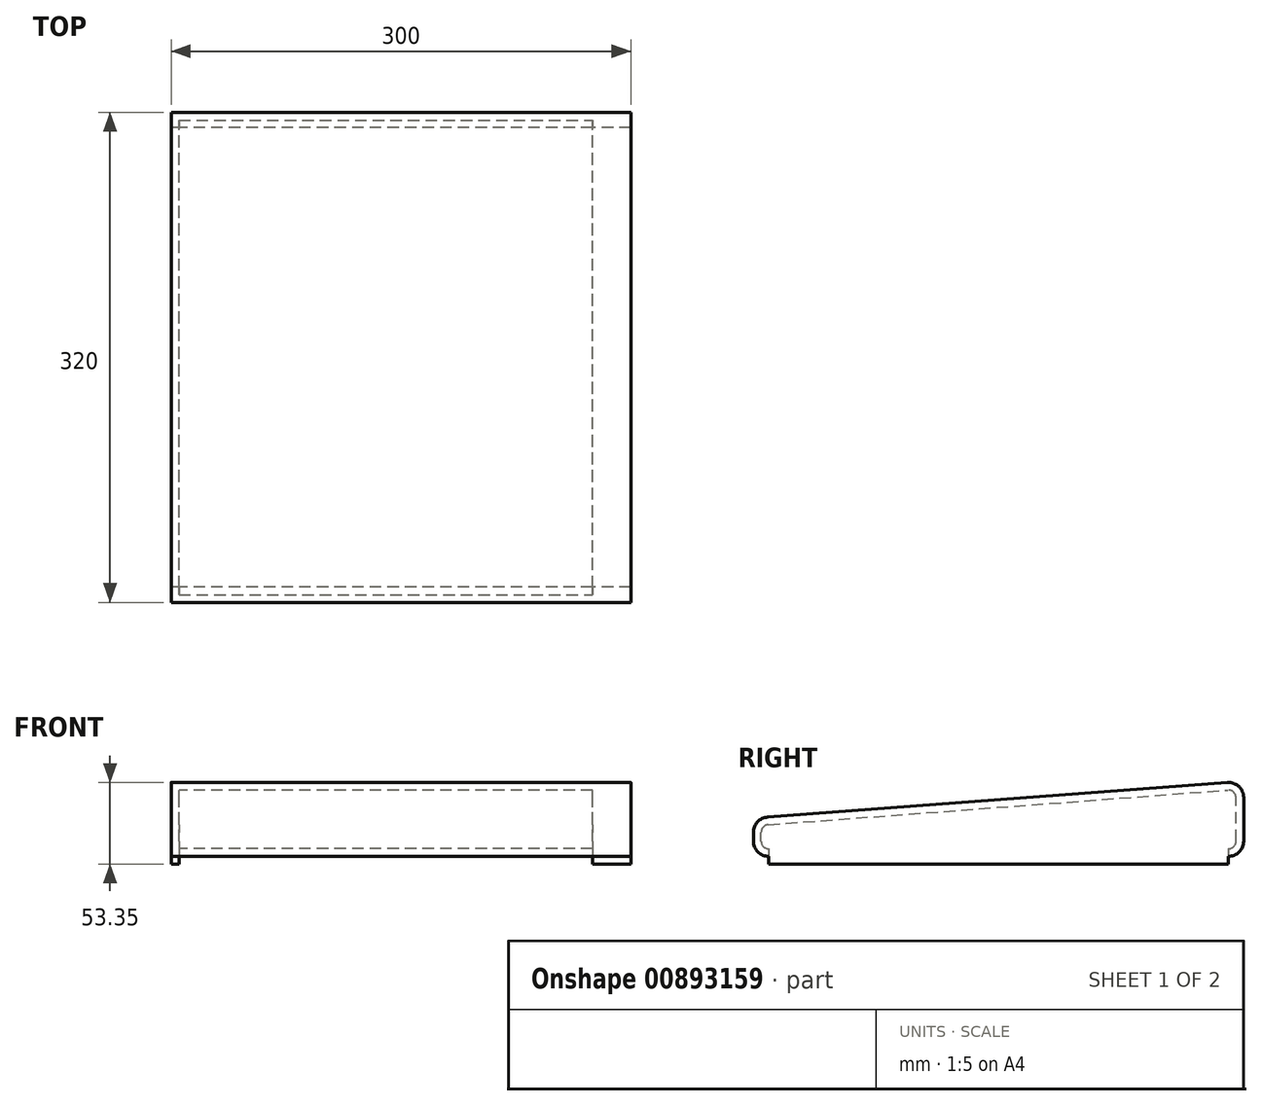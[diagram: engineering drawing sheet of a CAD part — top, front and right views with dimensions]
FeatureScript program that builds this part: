
annotation { "Feature Type Name" : "Feature", "Feature Type Description" : "" }
export const myFeature = defineFeature(function(context is Context, id is Id, definition is map)
    precondition{}
    {
        {
            var Q0;
            Q0=qCreatedBy(makeId("Right.planeOp"),FACE);
            var sketch = newSketch(context, id + "F0", { "sketchPlane" : qUnion([Q0])});
            skLineSegment(sketch, "E0", {"start": v(-351.34, -25) * mm, "end": v(-51.34, -25) * mm});
            skLineSegment(sketch, "E1", {"start": v(-361.34, -15) * mm, "end": v(-361.34, -9.27) * mm});
            skLineSegment(sketch, "E2", {"start": v(-41.34, -15) * mm, "end": v(-41.34, 13.35) * mm});
            skLineSegment(sketch, "E3", {"start": v(-352.1, 0.7) * mm, "end": v(-52.1, 23.32) * mm});
            skPoint(sketch, "E4.visualSharp", {"position": v(-361.34, 0) * mm});
            skArc(sketch, "E4.filletArc", {"start": v(-352.1, 0.7) * mm, "mid": v(-358.67, -2.47) * mm, "end": v(-361.34, -9.27) * mm});
            skPoint(sketch, "E5.visualSharp", {"position": v(-361.34, -25) * mm});
            skArc(sketch, "E5.filletArc", {"start": v(-361.34, -15) * mm, "mid": v(-358.4, -22.07) * mm, "end": v(-351.34, -25) * mm});
            skPoint(sketch, "E6.visualSharp", {"position": v(-41.34, 24.14) * mm});
            skArc(sketch, "E6.filletArc", {"start": v(-41.34, 13.35) * mm, "mid": v(-44.54, 20.69) * mm, "end": v(-52.1, 23.32) * mm});
            skPoint(sketch, "E7.visualSharp", {"position": v(-41.34, -25) * mm});
            skArc(sketch, "E7.filletArc", {"start": v(-51.34, -25) * mm, "mid": v(-44.27, -22.07) * mm, "end": v(-41.34, -15) * mm});
            skSolve(sketch);
        }
        {
            var Q0;
            Q0=makeQuery(id+"F0.imprint","IMPRINT",FACE,{"disambiguationData":[TD([[makeQuery(id+"F0.imprint","IMPRINT",EDGE,{"derivedFrom":sQuery(id+"F0.wireOp",EDGE,"E0")}),1.0]])]});
            extrude(context, id + "F1", {"entities" : qUnion([Q0]), "depth" : 300 * mm, "offsetDistance" : 25 * mm});
        }
        {
            var Q0;
            Q0=makeQuery(id+"F1.opExtrude","SWEPT_FACE",FACE,{"disambiguationData":[OSD([sQuery(id+"F0.wireOp",EDGE,"E0")])]});
            shell(context, id + "F2", {"entities" : qUnion([Q0]), "thickness" : 5 * mm});
        }
        {
            var Q0;
            Q0=makeQuery(id+"F1.opExtrude","CAP_FACE",FACE,{"disambiguationData":[OSD([sQuery(id+"F0.wireOp",EDGE,"E0"),sQuery(id+"F0.wireOp",EDGE,"E1"),sQuery(id+"F0.wireOp",EDGE,"E2"),sQuery(id+"F0.wireOp",EDGE,"E3"),sQuery(id+"F0.wireOp",EDGE,"E4.filletArc"),sQuery(id+"F0.wireOp",EDGE,"E5.filletArc"),sQuery(id+"F0.wireOp",EDGE,"E6.filletArc"),sQuery(id+"F0.wireOp",EDGE,"E7.filletArc")])],"isStart":false});
            var sketch = newSketch(context, id + "F3", { "sketchPlane" : qUnion([Q0])});
            skSolve(sketch);
        }
        {
            var Q0;
            Q0=makeQuery(id+"FV86FQ9cfDMdF77_1.boolean.opBoolean","SPLIT",FACE,{"disambiguationData":[TD([makeQuery(id+"FV86FQ9cfDMdF77_1.opExtrude","SWEPT_FACE",FACE,{"disambiguationData":[OSD([sQuery(id+"F3.wireOp",EDGE,"lBtMn5sw-AZNF-spVU-DaEl-DQMSO4VxvqlR")])]})])],"derivedFrom":makeQuery(id+"F1.opExtrude","CAP_FACE",FACE,{"disambiguationData":[OSD([sQuery(id+"F0.wireOp",EDGE,"E0"),sQuery(id+"F0.wireOp",EDGE,"E1"),sQuery(id+"F0.wireOp",EDGE,"E2"),sQuery(id+"F0.wireOp",EDGE,"E3"),sQuery(id+"F0.wireOp",EDGE,"E4.filletArc"),sQuery(id+"F0.wireOp",EDGE,"E5.filletArc"),sQuery(id+"F0.wireOp",EDGE,"E6.filletArc"),sQuery(id+"F0.wireOp",EDGE,"E7.filletArc")])],"isStart":false})});
            extrude(context, id + "F4", {"entities" : qUnion([Q0]), "operationType" : NewBodyOperationType.ADD, "oppositeDirection" : true, "depth" : 25 * mm, "offsetDistance" : 25 * mm});
        }
        {
            var Q0;
            Q0=makeQuery(id+"F2.opShell","OFFSET_FACE",FACE,{"disambiguationData":[OSD([sQuery(id+"F0.wireOp",EDGE,"E3")])]});
            var sketch = newSketch(context, id + "F5", { "sketchPlane" : qUnion([Q0])});
            skSolve(sketch);
        }
        {
            var Q0;
            Q0=qSketchRegion(id+"F5",true);
            var Q1;
            Q1=makeQuery(id+"F2.opShell","OFFSET_FACE",FACE,{"disambiguationData":[OSD([sQuery(id+"F0.wireOp",EDGE,"E0")])]});
            extrude(context, id + "F6", {"entities" : qUnion([Q0, Q1]), "operationType" : NewBodyOperationType.ADD, "depth" : 5 * mm, "offsetDistance" : 25 * mm});
        }
        {
            var Q0;
            Q0=makeQuery(id+"F1.opExtrude","SWEPT_FACE",FACE,{"disambiguationData":[OSD([sQuery(id+"F0.wireOp",EDGE,"E0")])]});
            extrude(context, id + "F7", {"entities" : qUnion([Q0]), "operationType" : NewBodyOperationType.ADD, "depth" : 5 * mm, "offsetDistance" : 25 * mm});
        }
        {
            var Q0;
            Q0=qCreatedBy(makeId("Right.planeOp"),FACE);
            cPlane(context, id + "F8", {"entities" : qUnion([Q0]), "cplaneType" : CPlaneType.OFFSET, "offset" : 13 * mm, "width" : 150 * mm, "height" : 150 * mm});
        }
        {
            var Q0;
            Q0 = qSketchRegion(id + "F0", true);
            var Q1;
            {var subQ0=sQuery(id+"F0.wireOp",EDGE,"E0");Q1=makeQuery(id+"F6.boolean.opBoolean","MERGE",FACE,{"derivedFrom":[makeQuery(id+"F1.opExtrude","CAP_FACE",FACE,{"disambiguationData":[OSD([subQ0,sQuery(id+"F0.wireOp",EDGE,"E1"),sQuery(id+"F0.wireOp",EDGE,"E2"),sQuery(id+"F0.wireOp",EDGE,"E3"),sQuery(id+"F0.wireOp",EDGE,"E4.filletArc"),sQuery(id+"F0.wireOp",EDGE,"E5.filletArc"),sQuery(id+"F0.wireOp",EDGE,"E6.filletArc"),sQuery(id+"F0.wireOp",EDGE,"E7.filletArc")])],"isStart":true}),makeQuery(id+"F6.opExtrude","SWEPT_FACE",FACE,{"disambiguationData":[OSD([subQ0]),TDD([makeQuery(id+"F1.opExtrude","CAP_EDGE",EDGE,{"disambiguationData":[OSD([subQ0])],"isStart":true})])]})]});}
            extrude(context, id + "F9", {"entities" : qUnion([Q0, Q1]), "operationType" : NewBodyOperationType.REMOVE, "oppositeDirection" : true, "depth" : 300 * mm, "offsetDistance" : 25 * mm});
        }
    });
